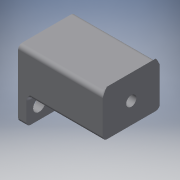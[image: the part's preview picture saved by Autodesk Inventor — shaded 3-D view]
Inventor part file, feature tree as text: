
AUTODESK INVENTOR PART (.ipt)
format: ipt  version: 2018 (Build 220112000, 112)  size: 438,784 bytes
history: native  units: in
note: dims shown in document units (in); Inventor stores cm internally (conversion verified against a paired STEP export)
features: reference x18, extrude x13, sketch x13, fillet x8, other x7, projected_geometry x4, plane x3
ambient origin geometry x8: Origin, YZ Plane, XZ Plane, XY Plane, X Axis, Y Axis, Z Axis, Center Point
bodies: Solid1 (feature_tree)
feature tree (66):
  extrude  "Extrusion1"  Depth=0.125in
  extrude  "Extrusion2"  Depth=0.4724in TaperAngle=0.0deg
  extrude  "Extrusion3"  Depth=0.2in TaperAngle=0.0deg
  extrude  "Extrusion4"  Depth=0.4in
  extrude  "Extrusion5"  Depth=0.25in
  extrude  "Extrusion6"  Depth=0.1181in TaperAngle=0.0deg
  fillet  "Fillet1"  Radius=0.125in
  fillet  "Fillet4"  Radius=0.1181in
  sketch  "Sketch8"  dims[d19=0.125in d20=0.1181in]
  plane  "Work Plane1"
  extrude  "Extrusion7"  Depth=0.1181in
  sketch  "Sketch9"  dims[d21=1.15in d22=0.0787in d23=0.0in d24=0.0394in d27=0.0394in d28=0.0197in d29=0.0197in]
  plane  "Work Plane2"
  extrude  "Extrusion8"  Depth=0.0394in TaperAngle=0.0deg
  fillet  "Fillet5"  Radius=0.0394in
  fillet  "Fillet6"  Radius=0.0394in
  fillet  "Fillet7"  Radius=0.0197in
  fillet  "Fillet9"  Radius=0.0197in
  sketch  "Sketch10"  dims[d30=1.0in d31=0.0in d32=0.0394in d33=0.0394in d34=1.0in d35=0.0in]
  plane  "Work Plane3"
  extrude  "Extrusion9"  Depth=0.0394in
  fillet  "Fillet10"  Radius=0.0394in
  fillet  "Fillet11"  Radius=1.0in
  extrude  "Extrusion10"  Depth=0.0394in
  extrude  "Extrusion11"  Depth=0.0394in
  extrude  "Extrusion12"  Depth=1.0in TaperAngle=0.0deg
  extrude  "Extrusion13"  Depth=0.0394in
  sketch  "Sketch1"  dims[d0=0.5in d1=0.125in]
  reference  "Reference1"
  reference  "Reference2"
  reference  "Reference3"
  reference  "Reference4"
  reference  "Reference5"
  reference  "Reference6"
  reference  "Reference7"
  reference  "Reference8"
  reference  "Reference9"
  reference  "Reference10"
  reference  "Reference11"
  reference  "Reference12"
  reference  "Reference13"
  reference  "Reference14"
  reference  "Reference15"
  reference  "Reference16"
  reference  "Reference17"
  sketch  "Sketch2"  dims[d2=0.7in d3=0.4724in d4=0.0in]
  projected_geometry  "Projected Loop1"
  projected_geometry  "Projected Loop2"
  sketch  "Sketch4"  dims[d5=0.0787in d6=0.0in d7=0.2in d8=0.0in]
  projected_geometry  "Projected Loop3"
  sketch  "Sketch5"  dims[d9=0.4in d10=0.4in]
  reference  "Reference20"
  sketch  "Sketch6"  dims[d11=0.5512in d12=0.0in d13=0.25in]
  sketch  "Sketch7"  dims[d14=0.25in d15=0.0787in d16=0.0in d17=0.125in d18=0.1181in]
  projected_geometry  "Projected Loop4"
  sketch  "Sketch11"  dims[d36=0.0394in d37=0.0394in]
  sketch  "Sketch12"  dims[d38=0.0394in d40=0.0394in]
  sketch  "Sketch13"  dims[d41=0.0098in d42=1.0in d43=0.0in]
  sketch  "Sketch14"  dims[d44=0.0394in d45=0.0394in d46=12.0in d47=0.0in d48=12.0in d49=0.0in d50=0.1969in d51=0.2362in d52=0.7087in d53=0.0in d54=0.128in d55=0.7087in d56=0.0in]
  other  "<userpath>\OneDrive\Documents\Inventor\TSA\2018\Animatronics\Tortoise\TurtleAssembly.iam"
  other  "TurtleAssembly.iam"
  other  "servo (2):1"
  other  "smallergear:4"
  other  "<userpath>\OneDrive\Documents\Inventor\TSA\2018\Animatronics\Tortoise\AssemblyTURTLE.iam"
  other  "AssemblyTURTLE.iam"
  other  "Frame:1"
